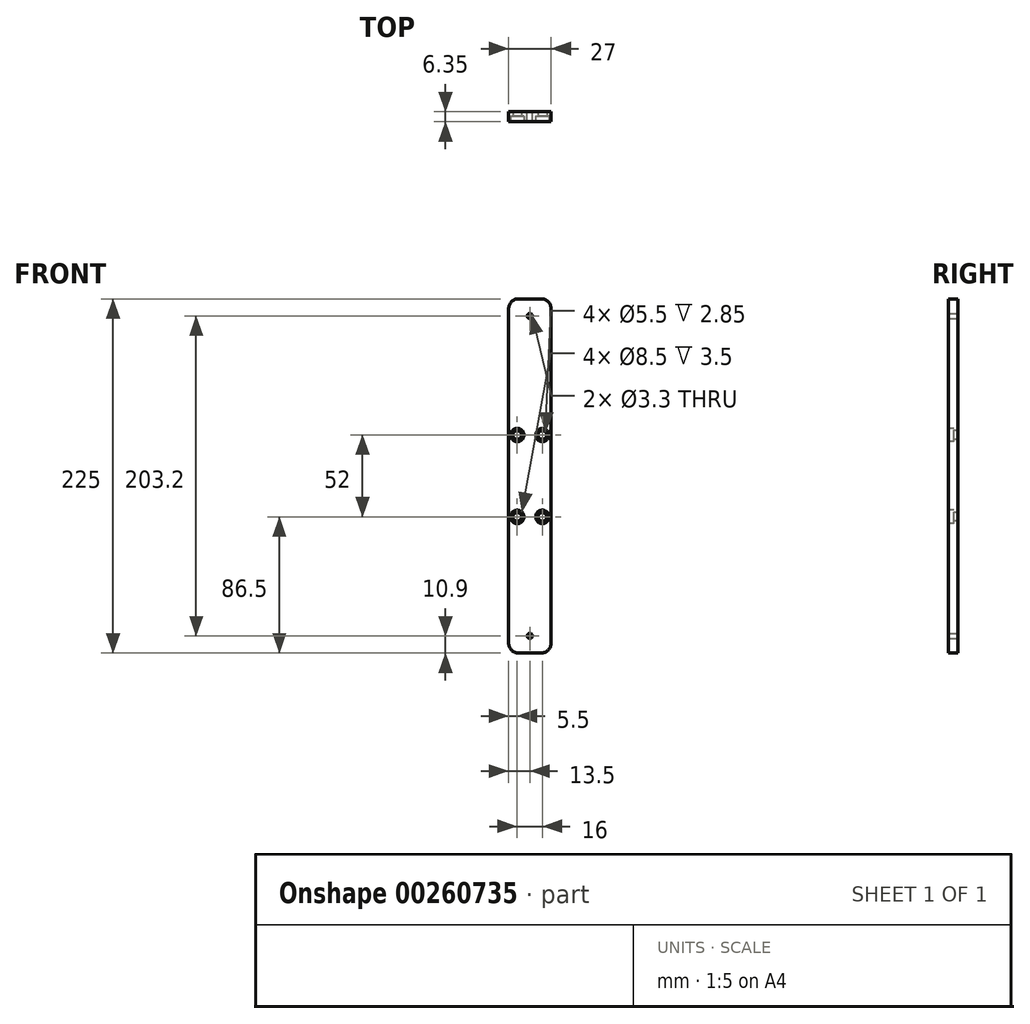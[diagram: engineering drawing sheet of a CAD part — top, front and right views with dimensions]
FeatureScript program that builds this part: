
annotation { "Feature Type Name" : "Feature", "Feature Type Description" : "" }
export const myFeature = defineFeature(function(context is Context, id is Id, definition is map)
    precondition{}
    {
        {
            var Q0;
            Q0=qCreatedBy(makeId("Front.planeOp"),FACE);
            var sketch = newSketch(context, id + "F0", { "sketchPlane" : qUnion([Q0])});
            skLineSegment(sketch, "E0.bottom", {"start": v(13.5, -112.5) * mm, "end": v(-13.5, -112.5) * mm});
            skLineSegment(sketch, "E0.top", {"start": v(13.5, 112.5) * mm, "end": v(-13.5, 112.5) * mm});
            skLineSegment(sketch, "E0.left", {"start": v(13.5, -112.5) * mm, "end": v(13.5, 112.5) * mm});
            skLineSegment(sketch, "E0.right", {"start": v(-13.5, -112.5) * mm, "end": v(-13.5, 112.5) * mm});
            skPoint(sketch, "E0.middle", {"position": v(0, 0) * mm});
            skSolve(sketch);
        }
        {
            var Q0;
            Q0=makeQuery(id+"F0.imprint","IMPRINT",FACE,{"disambiguationData":[TD([[makeQuery(id+"F0.imprint","IMPRINT",EDGE,{"derivedFrom":sQuery(id+"F0.wireOp",EDGE,"E0.bottom")}),-1.0]])]});
            extrude(context, id + "F1", {"entities" : qUnion([Q0]), "depth" : 6.35 * mm});
        }
        {
            var Q0;
            Q0=makeQuery(id+"F1.opExtrude","SWEPT_EDGE",EDGE,{"disambiguationData":[OSD([sQuery(id+"F0.wireOp",EDGE,"E0.top"),sQuery(id+"F0.wireOp",EDGE,"E0.left")])]});
            var Q1;
            Q1=makeQuery(id+"F1.opExtrude","SWEPT_EDGE",EDGE,{"disambiguationData":[OSD([sQuery(id+"F0.wireOp",EDGE,"E0.top"),sQuery(id+"F0.wireOp",EDGE,"E0.right")])]});
            var Q2;
            Q2=makeQuery(id+"F1.opExtrude","SWEPT_EDGE",EDGE,{"disambiguationData":[OSD([sQuery(id+"F0.wireOp",EDGE,"E0.bottom"),sQuery(id+"F0.wireOp",EDGE,"E0.left")])]});
            var Q3;
            Q3=makeQuery(id+"F1.opExtrude","SWEPT_EDGE",EDGE,{"disambiguationData":[OSD([sQuery(id+"F0.wireOp",EDGE,"E0.bottom"),sQuery(id+"F0.wireOp",EDGE,"E0.right")])]});
            fillet(context, id + "F2", {"entities" : qUnion([Q0, Q1, Q2, Q3]), "radius" : 6.35 * mm, "tangentPropagation" : true, "allowEdgeOverflow" : false});
        }
        {
            var Q0;
            Q0=makeQuery(id+"F1.opExtrude","CAP_FACE",FACE,{"disambiguationData":[OSD([sQuery(id+"F0.wireOp",EDGE,"E0.bottom"),sQuery(id+"F0.wireOp",EDGE,"E0.top"),sQuery(id+"F0.wireOp",EDGE,"E0.left"),sQuery(id+"F0.wireOp",EDGE,"E0.right")])],"isStart":false});
            var sketch = newSketch(context, id + "F3", { "sketchPlane" : qUnion([Q0])});
            skPoint(sketch, "E1", {"position": v(-8, 26) * mm});
            skPoint(sketch, "E2", {"position": v(-8, -26) * mm});
            skPoint(sketch, "E3", {"position": v(8, 26) * mm});
            skPoint(sketch, "E4", {"position": v(8, -26) * mm});
            skSolve(sketch);
        }
        {
            var Q0;
            Q0=sQuery(id+"F3.wireOp",VERTEX,"E1");
            var Q1;
            Q1=sQuery(id+"F3.wireOp",VERTEX,"E3");
            var Q2;
            Q2=sQuery(id+"F3.wireOp",VERTEX,"E2");
            var Q3;
            Q3=sQuery(id+"F3.wireOp",VERTEX,"E4");
            var Q4;
            Q4=makeQuery(id+"F1.opExtrude","SWEPT_BODY",BODY,{"disambiguationData":[OSD([sQuery(id+"F0.wireOp",EDGE,"E0.bottom"),sQuery(id+"F0.wireOp",EDGE,"E0.top"),sQuery(id+"F0.wireOp",EDGE,"E0.left"),sQuery(id+"F0.wireOp",EDGE,"E0.right")])]});
            hole(context, id + "F4", {"style" : HoleStyle.C_BORE, "endStyle" : HoleEndStyle.THROUGH, "holeDiameter" : 5.5 * mm, "cBoreDiameter" : 8.5 * mm, "cBoreDepth" : 3.5 * mm, "tappedDepth" : 12.7 * mm, "tapClearance" : 3, "locations" : qUnion([Q0, Q1, Q2, Q3]), "scope" : qUnion([Q4])});
        }
        {
            var Q0;
            Q0=makeQuery(id+"F1.opExtrude","CAP_FACE",FACE,{"disambiguationData":[OSD([sQuery(id+"F0.wireOp",EDGE,"E0.bottom"),sQuery(id+"F0.wireOp",EDGE,"E0.top"),sQuery(id+"F0.wireOp",EDGE,"E0.left"),sQuery(id+"F0.wireOp",EDGE,"E0.right")])],"isStart":true});
            var sketch = newSketch(context, id + "F5", { "sketchPlane" : qUnion([Q0])});
            skPoint(sketch, "E5", {"position": v(0, 101.6) * mm});
            skPoint(sketch, "E6", {"position": v(0, -101.6) * mm});
            skSolve(sketch);
        }
        {
            var Q0;
            Q0=sQuery(id+"F5.wireOp",VERTEX,"E5");
            var Q1;
            Q1=sQuery(id+"F5.wireOp",VERTEX,"E6");
            var Q2;
            Q2=makeQuery(id+"F1.opExtrude","SWEPT_BODY",BODY,{"disambiguationData":[OSD([sQuery(id+"F0.wireOp",EDGE,"E0.bottom"),sQuery(id+"F0.wireOp",EDGE,"E0.top"),sQuery(id+"F0.wireOp",EDGE,"E0.left"),sQuery(id+"F0.wireOp",EDGE,"E0.right")])]});
            hole(context, id + "F6", {"style" : HoleStyle.SIMPLE, "endStyle" : HoleEndStyle.THROUGH, "standardTappedOrClearance" : lookupTablePath({ "standard" : "ISO", "engagement" : "75%", "pitch" : "0.7 mm", "size" : "M4", "type" : "Tapped" }), "standardBlindInLast" : lookupTablePath({ "standard" : "ISO", "engagement" : "75%", "pitch" : "0.7 mm", "size" : "M4", "type" : "Tapped" }), "holeDiameter" : 3.3 * mm, "showTappedDepth" : true, "tappedDepth" : 12.7 * mm, "tapClearance" : 3, "locations" : qUnion([Q0, Q1]), "scope" : qUnion([Q2]), "majorDiameter" : 4 * mm});
        }
    });
